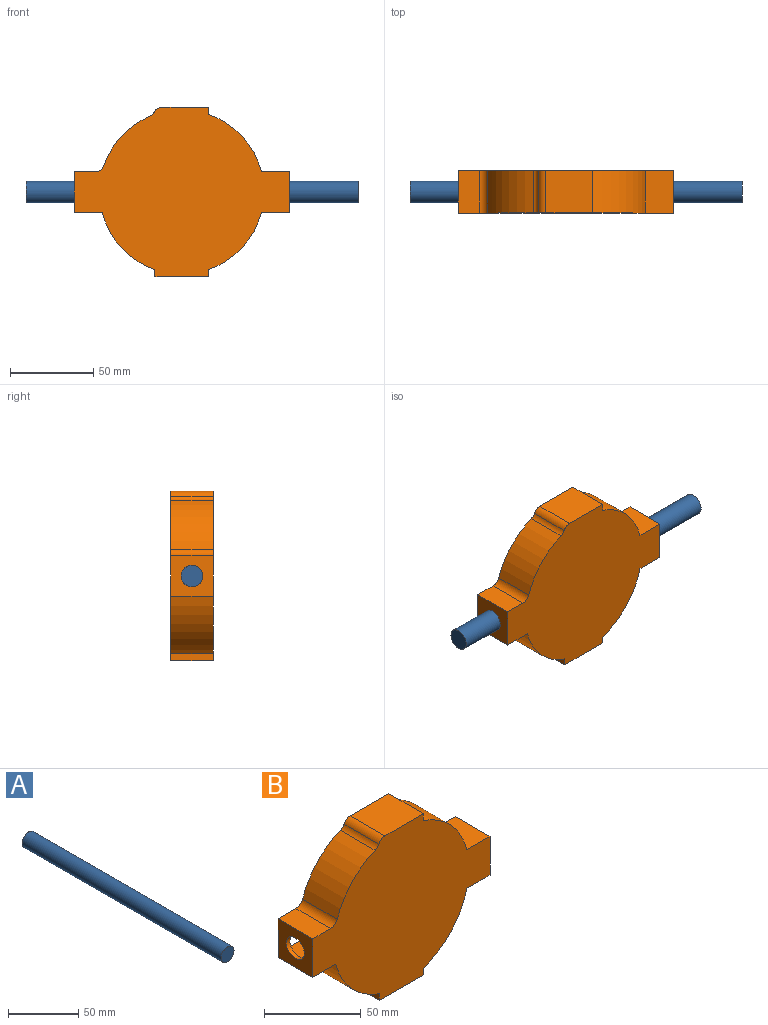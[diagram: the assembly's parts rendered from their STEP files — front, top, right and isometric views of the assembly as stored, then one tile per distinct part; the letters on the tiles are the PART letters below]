
ASSEMBLY  parts=2 mates=1
PART A: 3 faces, bbox 13x200x13 mm
  f0: cylinder r=6.5mm len=200mm, axis (0,1,0), area 8168.1mm2, adj f1,f2
  f1: plane 13x13mm, normal (0,-1,0), area 132.7mm2, adj f0
  f2: plane 13x13mm, normal (0,1,0), area 132.7mm2, adj f0
PART B: 41 faces, bbox 129.7x25.4x102.2 mm
  f0: plane 25.4x4.31mm, normal (1,0,0), area 109.5mm2, adj f1,f14,f15,f16
  f1: cylinder r=49.5mm len=34.53mm, axis (0,-1,0), area 1242.2mm2, adj f0,f2,f15,f16
  f2: plane 25.4x16.91mm, normal (0,0,1), area 429.5mm2, adj f1,f3,f15,f16
  f3: plane 25.4x24.51mm, normal (1,0,0), area 489.9mm2, adj f2,f4,f15,f16,f40
  f4: plane 25.4x16.91mm, normal (0,0,-1), area 429.5mm2, adj f3,f5,f15,f16
  f5: cylinder r=49.5mm len=34.53mm, axis (0,-1,0), area 1242.2mm2, adj f4,f6,f15,f16
  f6: plane 25.4x4.31mm, normal (1,0,0), area 109.5mm2, adj f5,f7,f15,f16
  f7: plane 32.31x25.4mm, normal (0,0,-1), area 820.8mm2, adj f6,f8,f15,f16
  f8: plane 25.4x4.31mm, normal (-1,0,0), area 109.5mm2, adj f7,f9,f15,f16
  f9: cylinder r=49.5mm len=34.53mm, axis (0,-1,0), area 1242.2mm2, adj f8,f10,f15,f16
  f10: plane 25.4x16.91mm, normal (0,0,-1), area 429.5mm2, adj f9,f11,f15,f16
  f11: plane 25.4x24.51mm, normal (-1,0,0), area 489.9mm2, adj f10,f12,f15,f16,f39
  f12: plane 25.4x13.12mm, normal (0,0,1), area 333.1mm2, adj f11,f15,f16,f33
  f13: cylinder r=49.5mm len=29.87mm, axis (0,-1,0), area 1066mm2, adj f15,f16,f33,f34
  f14: plane 28.17x25.4mm, normal (0,0,1), area 715.5mm2, adj f0,f15,f16,f38
  f15: plane 129.73x102.19mm, normal (0,1,0), area 974.3mm2, adj f0,f1,f2,f3,f4,f5,f6,f7
  f16: plane 129.73x102.19mm, normal (0,-1,0), area 8638.6mm2, adj f0,f1,f2,f3,f4,f5,f6,f7
  f17: plane 22.86x3.62mm, normal (-1,0,0), area 82.7mm2, adj f15,f18,f31,f32
  f18: cylinder r=46.96mm len=35.22mm, axis (0,-1,0), area 1146.6mm2, adj f15,f17,f19,f32
  f19: plane 22.86x16.39mm, normal (0,0,-1), area 374.6mm2, adj f15,f18,f20,f32
  f20: plane 22.86x19.43mm, normal (-1,0,0), area 311.5mm2, adj f15,f19,f21,f32,f40
  f21: plane 22.86x16.39mm, normal (0,0,1), area 374.6mm2, adj f15,f20,f22,f32
  f22: cylinder r=46.96mm len=35.22mm, axis (0,-1,0), area 1146.6mm2, adj f15,f21,f23,f32
  f23: plane 22.86x3.62mm, normal (-1,0,0), area 82.7mm2, adj f15,f22,f24,f32
  f24: plane 27.23x22.86mm, normal (0,0,1), area 622.6mm2, adj f15,f23,f25,f32
  f25: plane 22.86x3.62mm, normal (1,0,0), area 82.7mm2, adj f15,f24,f26,f32
  f26: cylinder r=46.96mm len=35.22mm, axis (0,-1,0), area 1146.6mm2, adj f15,f25,f27,f32
  f27: plane 22.86x16.39mm, normal (0,0,1), area 374.6mm2, adj f15,f26,f28,f32
  f28: plane 22.86x19.43mm, normal (1,0,0), area 311.5mm2, adj f15,f27,f29,f32,f39
  f29: plane 22.86x12.44mm, normal (0,0,-1), area 284.3mm2, adj f15,f28,f32,f35
  f30: cylinder r=46.96mm len=30.47mm, axis (0,-1,0), area 982.2mm2, adj f15,f32,f35,f36
  f31: plane 23.52x22.86mm, normal (0,0,-1), area 537.6mm2, adj f15,f17,f32,f37
  f32: plane 124.65x97.11mm, normal (0,1,0), area 7664.4mm2, adj f17,f18,f19,f20,f21,f22,f23,f24
  f33: cylinder r=5.08mm len=25.4mm, axis (0,-1,0), area 161mm2, adj f12,f13,f15,f16
  f34: cylinder r=5.08mm len=25.4mm, axis (0,-1,0), area 95.3mm2, adj f13,f15,f16,f38
  f35: cylinder r=5.08mm len=22.86mm, axis (0,-1,0), area 148.9mm2, adj f15,f29,f30,f32
  f36: cylinder r=5.08mm len=22.86mm, axis (0,1,0), area 78.9mm2, adj f15,f30,f32,f37
  f37: cylinder r=5.08mm len=22.86mm, axis (0,1,0), area 121.5mm2, adj f15,f31,f32,f36
  f38: cylinder r=5.08mm len=25.4mm, axis (0,-1,0), area 146.9mm2, adj f14,f15,f16,f34
  f39: cylinder r=6.5mm len=13mm, axis (1,0,0), area 103.7mm2, adj f11,f28
  f40: cylinder r=6.5mm len=13mm, axis (1,0,0), area 103.7mm2, adj f3,f20
PLACE A rot(axis=(0.58,-0.58,0.58),120deg) t=(-93.86,-47.08,78.03)mm
PLACE B t=(0,-34.38,78.03)mm
MATE slider A.f0 <-> B.f39  axis (-1,0,0) through (6.14,-47.08,78.03)mm
